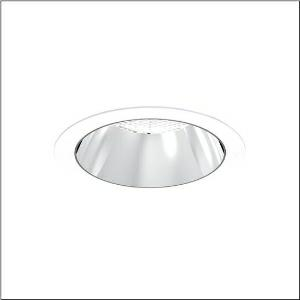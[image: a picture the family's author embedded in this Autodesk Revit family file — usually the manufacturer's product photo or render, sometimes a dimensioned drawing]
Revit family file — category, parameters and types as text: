
# Revit family: lunis_21_xl_51db15ef91c
name_source: partatom
category: Lighting Fixtures
units: mm (PartAtom-declared; Revit-internal decimal feet)

## family parameters
Cut with Voids When Loaded = No
Host = Face
Light Source = No
Part Type = Normal
Room Calculation Point = No
Round Connector Dimension = Use Diameter
Shared = No

## types (1)
- --- (1 x LED, 4110 lm, 25.4 W, 6500K)
    Apparent Load = 25 VA
    CIE Flux Codes = 92 100 100 100 100
    Color Rendering = 80
    Color Temperature = 6500K
    Default Elevation = 1800 mm
    Description = Lunis 21,  XL, downlight, light control with lens, of PMMA, anti glare with reflector, of PC, highly specular, light emission: direct distribution, LED rated luminous flux: 2.430lm, light colour: 830/840/865, with terminal, 5-pole, mains connection: 220..240V, AC/DC, 0/50..60Hz, housing, round, of diecast aluminium, traffic white (RAL 9016), diameter: 230mm, clamping range: 1..40mm, protection rating (complete): IP20, protection rating (on room side): IP54, insulation class (complete): insulation class II (safety insulation), certification: CE, impact resistance: IK03, packaging unit: 1 piece
    Height = 0 mm  [stored 0 ft]
    Lamp = 1 x LED
    Lamp Light Flux = 4110 lm
    Lamp Power = 25.4 W
    Lamp count = 1
    Length = 230 mm
    Luminous efficacy = 162 lm/W
    Manufacturer = Siteco
    ModVariant = No
    Model = 51DB15EF91C
    Mounting Place = Ceiling
    Mounting Type = Recessed
    Number of Poles = 1
    OnlyDefault = Yes
    Power Factor = 1
    Product Name = Lunis 21 XL
    Product group = downlight
    ProductGroupID = 400
    Protection Class = Protection class II
    Protection Degree = IP 20
    RLX_Detail_Level = 1
    RLX_Emergency_Light_Flux = 0 lm
    RLX_Emergency_Type = 0
    RLX_Emergency_Type_DB = No
    RlxData = <blob elided: 22237 chars, md5=87b227c9>
    Socket = socket
    Standby Power = 0 W
    System Light Flux = 4110 lm
    System Power = 25 W
    Type Comments = individual setting: colour temperature 6500K, luminous flux: 100 % | (ON | ON | OFF | OFF) | 700 mA
    Type Image = l_1291156.jpg
    URL = http://relux.com
    VarID = @adj_020266
    Voltage = 0 V
    Weight = 0.00 kg
    Width = 0 mm  [stored 0 ft]

note: [stored X ft] marks values corroborated as IEEE doubles in the binary element streams (Revit-internal decimal feet)

## geometry (parser evidence)
native form markers: Blend x4, Sweep x11
no freeform markers — native parametric forms only
